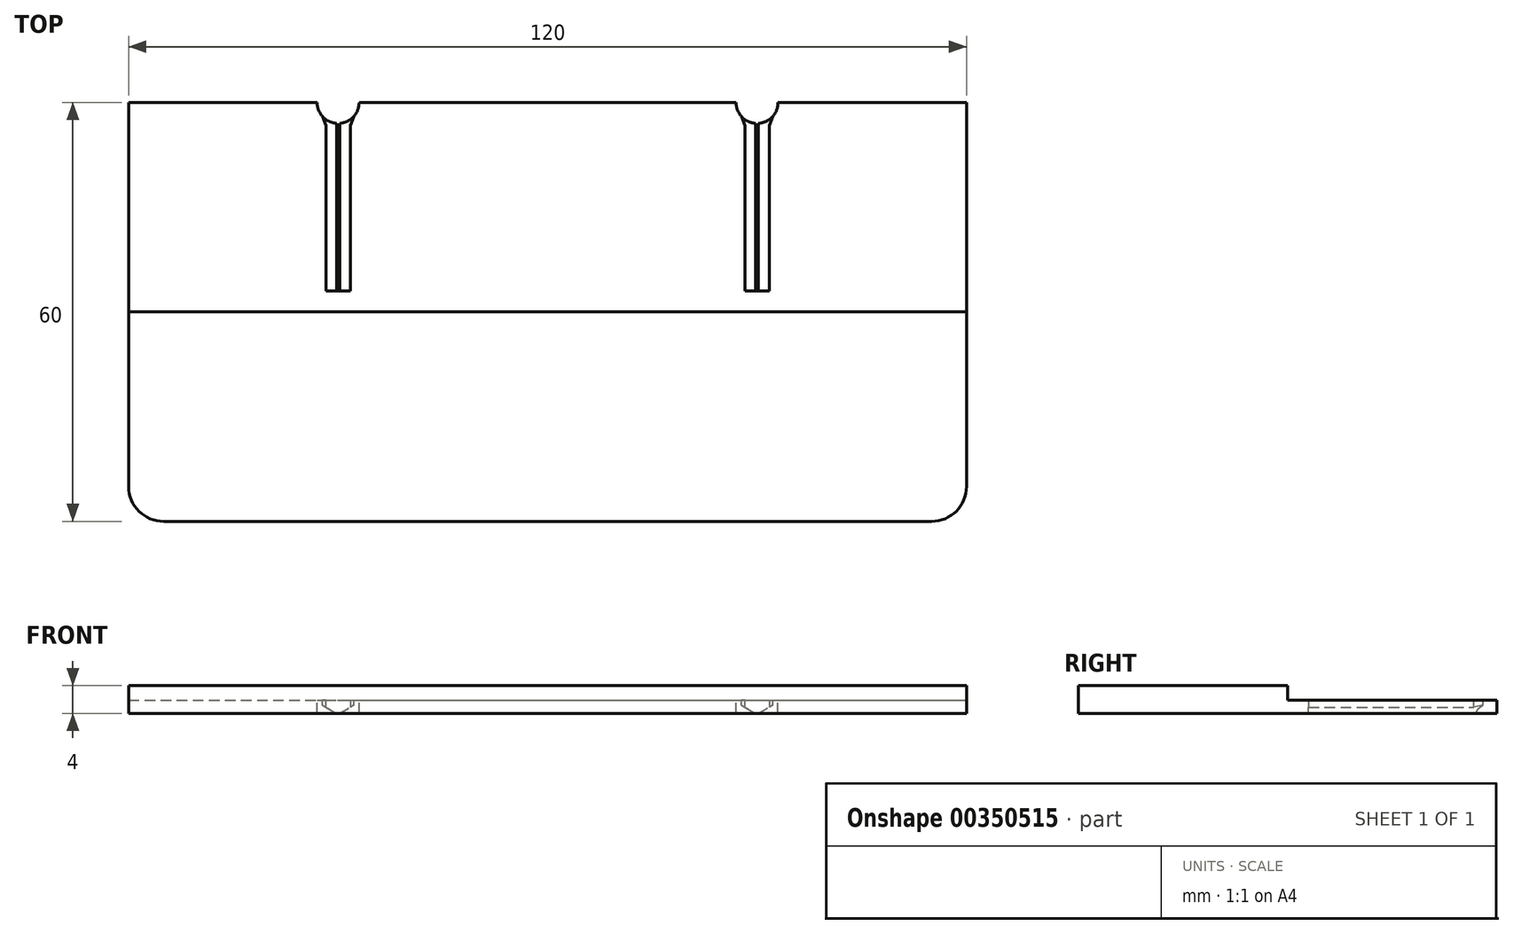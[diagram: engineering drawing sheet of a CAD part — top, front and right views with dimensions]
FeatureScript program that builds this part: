
annotation { "Feature Type Name" : "Feature", "Feature Type Description" : "" }
export const myFeature = defineFeature(function(context is Context, id is Id, definition is map)
    precondition{}
    {
        {
            var Q0;
            Q0=qCreatedBy(makeId("Top.planeOp"),FACE);
            var sketch = newSketch(context, id + "F0", { "sketchPlane" : qUnion([Q0])});
            skLineSegment(sketch, "E0.bottom", {"start": v(-60, 30) * mm, "end": v(60, 30) * mm});
            skLineSegment(sketch, "E0.top", {"start": v(-60, -30) * mm, "end": v(60, -30) * mm});
            skLineSegment(sketch, "E0.left", {"start": v(-60, 30) * mm, "end": v(-60, -30) * mm});
            skLineSegment(sketch, "E0.right", {"start": v(60, 30) * mm, "end": v(60, -30) * mm});
            skPoint(sketch, "E0.middle", {"position": v(0, 0) * mm});
            skSolve(sketch);
        }
        {
            var Q0;
            Q0=makeQuery(id+"F0.imprint","IMPRINT",FACE,{"disambiguationData":[TD([[makeQuery(id+"F0.imprint","IMPRINT",EDGE,{"derivedFrom":sQuery(id+"F0.wireOp",EDGE,"E0.bottom")}),-1.0]])]});
            var sketch = newSketch(context, id + "F1", { "sketchPlane" : qUnion([Q0])});
            skSolve(sketch);
        }
        {
            var Q0;
            Q0 = qSketchRegion(id + "F1", true);
            var Q1;
            Q1=makeQuery(id+"F0.imprint","IMPRINT",FACE,{"disambiguationData":[TD([[makeQuery(id+"F0.imprint","IMPRINT",EDGE,{"derivedFrom":sQuery(id+"F0.wireOp",EDGE,"E0.bottom")}),-1.0]])]});
            extrude(context, id + "F2", {"entities" : qUnion([Q0, Q1]), "depth" : 1.9 * mm});
        }
        {
            var Q0;
            Q0=makeQuery(id+"F2.opExtrude","CAP_FACE",FACE,{"disambiguationData":[OSD([sQuery(id+"F0.wireOp",EDGE,"E0.bottom"),sQuery(id+"F0.wireOp",EDGE,"E0.top"),sQuery(id+"F0.wireOp",EDGE,"E0.left"),sQuery(id+"F0.wireOp",EDGE,"E0.right")])],"isStart":false});
            var sketch = newSketch(context, id + "F3", { "sketchPlane" : qUnion([Q0])});
            skLineSegment(sketch, "E1.bottom", {"start": v(-60, -30) * mm, "end": v(60, -30) * mm});
            skLineSegment(sketch, "E1.top", {"start": v(-60, 0) * mm, "end": v(60, 0) * mm});
            skLineSegment(sketch, "E1.left", {"start": v(-60, -30) * mm, "end": v(-60, 0) * mm});
            skLineSegment(sketch, "E1.right", {"start": v(60, -30) * mm, "end": v(60, 0) * mm});
            skSolve(sketch);
        }
        {
            var Q0;
            Q0=makeQuery(id+"F3.imprint","IMPRINT",FACE,{"disambiguationData":[TD([[makeQuery(id+"F3.imprint","IMPRINT",EDGE,{"derivedFrom":sQuery(id+"F3.wireOp",EDGE,"E1.bottom")}),1.0]])]});
            extrude(context, id + "F4", {"entities" : qUnion([Q0]), "operationType" : NewBodyOperationType.ADD, "depth" : 2.1 * mm});
        }
        {
            var Q0;
            Q0=makeQuery(id+"F2.opExtrude","SWEPT_FACE",FACE,{"disambiguationData":[OSD([sQuery(id+"F0.wireOp",EDGE,"E0.bottom")])]});
            var sketch = newSketch(context, id + "F5", { "sketchPlane" : qUnion([Q0])});
            skLineSegment(sketch, "E2", {"start": v(-60, 1.9) * mm, "end": v(60, 1.9) * mm, "construction": true});
            skLineSegment(sketch, "E3", {"start": v(60, 1.9) * mm, "end": v(0, 1.9) * mm, "construction": true});
            skLineSegment(sketch, "E4", {"start": v(0, 1.9) * mm, "end": v(-60, 1.9) * mm, "construction": true});
            skLineSegment(sketch, "E5", {"start": v(-30, 1.9) * mm, "end": v(60, 1.9) * mm, "construction": true});
            skLineSegment(sketch, "E6", {"start": v(60, 1.9) * mm, "end": v(30, 1.9) * mm, "construction": true});
            skCircle(sketch, "E7.cCircle", {"center": v(-30, 1.9) * mm, "radius": 1.75 * mm, "construction": true});
            skLineSegment(sketch, "E7.0", {"start": v(-31.75, 0.89) * mm, "end": v(-31.75, 2.91) * mm});
            skLineSegment(sketch, "E7.1", {"start": v(-31.75, 2.91) * mm, "end": v(-30, 3.92) * mm});
            skLineSegment(sketch, "E7.2", {"start": v(-30, 3.92) * mm, "end": v(-28.25, 2.91) * mm});
            skLineSegment(sketch, "E7.3", {"start": v(-28.25, 2.91) * mm, "end": v(-28.25, 0.89) * mm});
            skLineSegment(sketch, "E7.4", {"start": v(-28.25, 0.89) * mm, "end": v(-30, -0.12) * mm});
            skLineSegment(sketch, "E7.5", {"start": v(-30, -0.12) * mm, "end": v(-31.75, 0.89) * mm});
            skPoint(sketch, "E7.0.midPoint", {"position": v(-31.75, 1.9) * mm});
            skSolve(sketch);
        }
        {
            var Q0;
            {var subQ0=sQuery(id+"F5.wireOp",EDGE,"E7.5");var subQ1=sQuery(id+"F5.wireOp",EDGE,"E7.0");var subQ2=makeQuery(id+"F5.imprint","INTERSECT",VERTEX,{"derivedFrom":[subQ1,subQ0]});Q0=makeQuery(id+"F5.imprint","IMPRINT",FACE,{"disambiguationData":[TD([[makeQuery(id+"F5.imprint","IMPRINT",EDGE,{"disambiguationData":[TD([[subQ2,-1.0]])],"derivedFrom":subQ1}),-1.0]])]});}
            extrude(context, id + "F6", {"entities" : qUnion([Q0]), "operationType" : NewBodyOperationType.REMOVE, "oppositeDirection" : true, "depth" : 27 * mm});
        }
        {
            var Q0;
            {var subQ0=sQuery(id+"F0.wireOp",EDGE,"E0.left");var subQ3=sQuery(id+"F0.wireOp",EDGE,"E0.bottom");Q0=makeQuery(id+"F6.boolean.opBoolean","SPLIT",FACE,{"disambiguationData":[TD([makeQuery(id+"F2.opExtrude","SWEPT_FACE",FACE,{"disambiguationData":[OSD([subQ0])]})])],"derivedFrom":makeQuery(id+"F2.opExtrude","SWEPT_FACE",FACE,{"disambiguationData":[OSD([subQ3])]})});}
            var sketch = newSketch(context, id + "F7", { "sketchPlane" : qUnion([Q0])});
            skLineSegment(sketch, "E8.bottom", {"start": v(0, 0) * mm, "end": v(60, 0) * mm, "construction": true});
            skLineSegment(sketch, "E8.top", {"start": v(0, 1.9) * mm, "end": v(60, 1.9) * mm, "construction": true});
            skLineSegment(sketch, "E8.left", {"start": v(0, 0) * mm, "end": v(0, 1.9) * mm, "construction": true});
            skLineSegment(sketch, "E8.right", {"start": v(60, 0) * mm, "end": v(60, 1.9) * mm, "construction": true});
            skCircle(sketch, "E9.cCircle", {"center": v(30, 1.9) * mm, "radius": 1.75 * mm, "construction": true});
            skLineSegment(sketch, "E9.0", {"start": v(28.25, 0.89) * mm, "end": v(28.25, 2.91) * mm, "construction": true});
            skLineSegment(sketch, "E9.1", {"start": v(28.25, 2.91) * mm, "end": v(30, 3.92) * mm, "construction": true});
            skLineSegment(sketch, "E9.2", {"start": v(30, 3.92) * mm, "end": v(31.75, 2.91) * mm, "construction": true});
            skLineSegment(sketch, "E9.3", {"start": v(31.75, 2.91) * mm, "end": v(31.75, 0.89) * mm, "construction": true});
            skLineSegment(sketch, "E9.4", {"start": v(31.75, 0.89) * mm, "end": v(30, -0.12) * mm, "construction": true});
            skLineSegment(sketch, "E9.5", {"start": v(30, -0.12) * mm, "end": v(28.25, 0.89) * mm, "construction": true});
            skPoint(sketch, "E9.0.midPoint", {"position": v(28.25, 1.9) * mm});
            skLineSegment(sketch, "E10.0", {"start": v(28.25, 0.89) * mm, "end": v(28.25, 2.91) * mm});
            skLineSegment(sketch, "E10.1", {"start": v(28.25, 2.91) * mm, "end": v(30, 3.92) * mm});
            skLineSegment(sketch, "E10.2", {"start": v(30, 3.92) * mm, "end": v(31.75, 2.91) * mm});
            skLineSegment(sketch, "E10.3", {"start": v(31.75, 2.91) * mm, "end": v(31.75, 0.89) * mm});
            skLineSegment(sketch, "E10.4", {"start": v(31.75, 0.89) * mm, "end": v(30, -0.12) * mm});
            skLineSegment(sketch, "E10.5", {"start": v(30, -0.12) * mm, "end": v(28.25, 0.89) * mm});
            skSolve(sketch);
        }
        {
            var Q0;
            {var subQ0=sQuery(id+"F7.wireOp",EDGE,"E10.5");var subQ1=sQuery(id+"F7.wireOp",EDGE,"E10.0");var subQ2=makeQuery(id+"F7.imprint","INTERSECT",VERTEX,{"derivedFrom":[subQ1,subQ0]});Q0=makeQuery(id+"F7.imprint","IMPRINT",FACE,{"disambiguationData":[TD([[makeQuery(id+"F7.imprint","IMPRINT",EDGE,{"disambiguationData":[TD([[subQ2,-1.0]])],"derivedFrom":subQ1}),-1.0]])]});}
            extrude(context, id + "F8", {"entities" : qUnion([Q0]), "operationType" : NewBodyOperationType.REMOVE, "oppositeDirection" : true, "depth" : 27 * mm});
        }
        {
            var Q0;
            Q0=makeQuery(id+"F4.boolean.opBoolean","MERGE",EDGE,{"derivedFrom":[makeQuery(id+"F2.opExtrude","SWEPT_EDGE",EDGE,{"disambiguationData":[OSD([sQuery(id+"F0.wireOp",EDGE,"E0.top"),sQuery(id+"F0.wireOp",EDGE,"E0.right")])]}),makeQuery(id+"F4.opExtrude","SWEPT_EDGE",EDGE,{"disambiguationData":[OSD([sQuery(id+"F3.wireOp",EDGE,"E1.bottom"),sQuery(id+"F3.wireOp",EDGE,"E1.right")])]})]});
            var Q1;
            Q1=makeQuery(id+"F4.boolean.opBoolean","MERGE",EDGE,{"derivedFrom":[makeQuery(id+"F2.opExtrude","SWEPT_EDGE",EDGE,{"disambiguationData":[OSD([sQuery(id+"F0.wireOp",EDGE,"E0.top"),sQuery(id+"F0.wireOp",EDGE,"E0.left")])]}),makeQuery(id+"F4.opExtrude","SWEPT_EDGE",EDGE,{"disambiguationData":[OSD([sQuery(id+"F3.wireOp",EDGE,"E1.bottom"),sQuery(id+"F3.wireOp",EDGE,"E1.left")])]})]});
            fillet(context, id + "F9", {"entities" : qUnion([Q0, Q1]), "radius" : 5 * mm, "tangentPropagation" : true, "allowEdgeOverflow" : false});
        }
        {
            var Q0;
            Q0=makeQuery(id+"F2.opExtrude","CAP_FACE",FACE,{"disambiguationData":[OSD([sQuery(id+"F0.wireOp",EDGE,"E0.bottom"),sQuery(id+"F0.wireOp",EDGE,"E0.top"),sQuery(id+"F0.wireOp",EDGE,"E0.left"),sQuery(id+"F0.wireOp",EDGE,"E0.right")])],"isStart":false});
            var sketch = newSketch(context, id + "F10", { "sketchPlane" : qUnion([Q0])});
            skLineSegment(sketch, "E11", {"start": v(-31.75, 3) * mm, "end": v(-28.25, 3) * mm, "construction": true});
            skPoint(sketch, "E12", {"position": v(-30, 3) * mm});
            skLineSegment(sketch, "E13", {"start": v(28.25, 3) * mm, "end": v(31.75, 3) * mm, "construction": true});
            skPoint(sketch, "E14", {"position": v(30, 3) * mm});
            skLineSegment(sketch, "E15", {"start": v(-30, 3) * mm, "end": v(-30, 30) * mm, "construction": true});
            skPoint(sketch, "E16", {"position": v(-30, 30) * mm});
            skLineSegment(sketch, "E17", {"start": v(30, 3) * mm, "end": v(30, 30) * mm, "construction": true});
            skPoint(sketch, "E18", {"position": v(30, 30) * mm});
            skCircle(sketch, "E19", {"center": v(30, 30) * mm, "radius": 3 * mm});
            skCircle(sketch, "E20", {"center": v(-30, 30) * mm, "radius": 3 * mm});
            skSolve(sketch);
        }
        {
            var Q0;
            Q0 = qSketchRegion(id + "F10", true);
            extrude(context, id + "F11", {"entities" : qUnion([Q0]), "operationType" : NewBodyOperationType.REMOVE, "oppositeDirection" : true, "depth" : 2 * mm});
        }
        {
            var Q0;
            Q0=makeQuery(id+"F11.boolean.opBoolean","INTERSECT",EDGE,{"derivedFrom":[makeQuery(id+"F6.boolean.opBoolean","COPY",FACE,{"derivedFrom":makeQuery(id+"F6.opExtrude","SWEPT_FACE",FACE,{"disambiguationData":[OSD([sQuery(id+"F5.wireOp",EDGE,"E7.3")])]})}),makeQuery(id+"F11.opExtrude","SWEPT_FACE",FACE,{"disambiguationData":[OSD([sQuery(id+"F10.wireOp",EDGE,"E19")])]})]});
            var Q1;
            Q1=makeQuery(id+"F11.boolean.opBoolean","INTERSECT",EDGE,{"derivedFrom":[makeQuery(id+"F6.boolean.opBoolean","COPY",FACE,{"derivedFrom":makeQuery(id+"F6.opExtrude","SWEPT_FACE",FACE,{"disambiguationData":[OSD([sQuery(id+"F5.wireOp",EDGE,"E7.0")])]})}),makeQuery(id+"F11.opExtrude","SWEPT_FACE",FACE,{"disambiguationData":[OSD([sQuery(id+"F10.wireOp",EDGE,"E19")])]})]});
            var Q2;
            Q2=makeQuery(id+"F11.boolean.opBoolean","INTERSECT",EDGE,{"derivedFrom":[makeQuery(id+"F8.boolean.opBoolean","COPY",FACE,{"derivedFrom":makeQuery(id+"F8.opExtrude","SWEPT_FACE",FACE,{"disambiguationData":[OSD([sQuery(id+"F7.wireOp",EDGE,"E10.3")])]})}),makeQuery(id+"F11.opExtrude","SWEPT_FACE",FACE,{"disambiguationData":[OSD([sQuery(id+"F10.wireOp",EDGE,"E20")])]})]});
            var Q3;
            Q3=makeQuery(id+"F11.boolean.opBoolean","INTERSECT",EDGE,{"derivedFrom":[makeQuery(id+"F8.boolean.opBoolean","COPY",FACE,{"derivedFrom":makeQuery(id+"F8.opExtrude","SWEPT_FACE",FACE,{"disambiguationData":[OSD([sQuery(id+"F7.wireOp",EDGE,"E10.0")])]})}),makeQuery(id+"F11.opExtrude","SWEPT_FACE",FACE,{"disambiguationData":[OSD([sQuery(id+"F10.wireOp",EDGE,"E20")])]})]});
            chamfer(context, id + "F12", {"entities" : qUnion([Q0, Q1, Q2, Q3]), "width" : 2 * mm, "tangentPropagation" : true});
        }
    });
